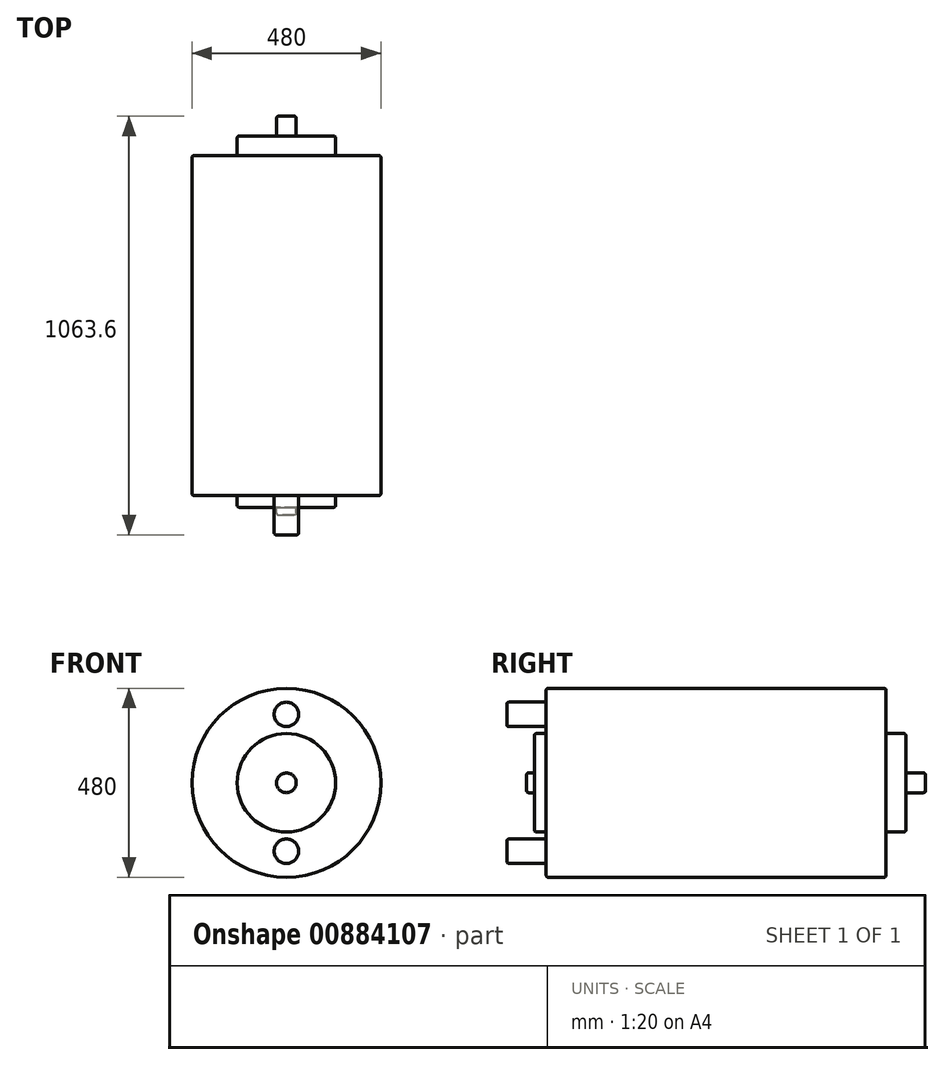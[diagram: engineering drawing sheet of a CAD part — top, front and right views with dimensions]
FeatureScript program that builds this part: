
annotation { "Feature Type Name" : "Feature", "Feature Type Description" : "" }
export const myFeature = defineFeature(function(context is Context, id is Id, definition is map)
    precondition{}
    {
        {
            var Q0;
            Q0=qCreatedBy(makeId("Right.planeOp"),FACE);
            var sketch = newSketch(context, id + "F0", { "sketchPlane" : qUnion([Q0])});
            skLineSegment(sketch, "E0", {"start": v(-50, 0) * mm, "end": v(-50, 25) * mm});
            skLineSegment(sketch, "E1", {"start": v(-50, 25) * mm, "end": v(-30, 25) * mm});
            skLineSegment(sketch, "E2", {"start": v(-30, 25) * mm, "end": v(-30, 125) * mm});
            skLineSegment(sketch, "E3", {"start": v(-30, 125) * mm, "end": v(0, 125) * mm});
            skLineSegment(sketch, "E4", {"start": v(0, 125) * mm, "end": v(0, 240) * mm});
            skLineSegment(sketch, "E5", {"start": v(0, 240) * mm, "end": v(863.6, 240) * mm});
            skLineSegment(sketch, "E6", {"start": v(863.6, 240) * mm, "end": v(863.6, 125) * mm});
            skLineSegment(sketch, "E7", {"start": v(863.6, 125) * mm, "end": v(913.6, 125) * mm});
            skLineSegment(sketch, "E8", {"start": v(913.6, 125) * mm, "end": v(913.6, 25) * mm});
            skLineSegment(sketch, "E9", {"start": v(913.6, 25) * mm, "end": v(963.6, 25) * mm});
            skLineSegment(sketch, "E10", {"start": v(963.6, 25) * mm, "end": v(963.6, 0) * mm});
            skLineSegment(sketch, "E11", {"start": v(963.6, 0) * mm, "end": v(-50, 0) * mm});
            skSolve(sketch);
        }
        {
            var Q0;
            Q0 = qSketchRegion(id + "F0", true);
            var Q1;
            Q1=sQuery(id+"F0.wireOp",EDGE,"E11");
            revolve(context, id + "F1", {"surfaceOperationType" : NewSurfaceOperationType.NEW, "entities" : qUnion([Q0]), "axis" : qUnion([Q1]), "revolveType" : RevolveType.FULL});
        }
        {
            var Q0;
            Q0=makeQuery(id+"F1.opRevolve","SWEPT_EDGE",EDGE,{"disambiguationData":[OSD([sQuery(id+"F0.wireOp",EDGE,"E5"),sQuery(id+"F0.wireOp",EDGE,"E6")])]});
            var Q1;
            Q1=makeQuery(id+"F1.opRevolve","SWEPT_EDGE",EDGE,{"disambiguationData":[OSD([sQuery(id+"F0.wireOp",EDGE,"E7"),sQuery(id+"F0.wireOp",EDGE,"E8")])]});
            var Q2;
            Q2=makeQuery(id+"F1.opRevolve","SWEPT_EDGE",EDGE,{"disambiguationData":[OSD([sQuery(id+"F0.wireOp",EDGE,"E9"),sQuery(id+"F0.wireOp",EDGE,"E10")])]});
            var Q3;
            Q3=makeQuery(id+"F1.opRevolve","SWEPT_EDGE",EDGE,{"disambiguationData":[OSD([sQuery(id+"F0.wireOp",EDGE,"E4"),sQuery(id+"F0.wireOp",EDGE,"E5")])]});
            var Q4;
            Q4=makeQuery(id+"F1.opRevolve","SWEPT_EDGE",EDGE,{"disambiguationData":[OSD([sQuery(id+"F0.wireOp",EDGE,"E2"),sQuery(id+"F0.wireOp",EDGE,"E3")])]});
            var Q5;
            Q5=makeQuery(id+"F1.opRevolve","SWEPT_EDGE",EDGE,{"disambiguationData":[OSD([sQuery(id+"F0.wireOp",EDGE,"E0"),sQuery(id+"F0.wireOp",EDGE,"E1")])]});
            fillet(context, id + "F2", {"entities" : qUnion([Q0, Q1, Q2, Q3, Q4, Q5]), "radius" : 5.08 * mm, "tangentPropagation" : true, "allowEdgeOverflow" : false});
        }
        {
            var Q0;
            Q0=makeQuery(id+"F1.opRevolve","SWEPT_FACE",FACE,{"disambiguationData":[OSD([sQuery(id+"F0.wireOp",EDGE,"E4")])]});
            var sketch = newSketch(context, id + "F3", { "sketchPlane" : qUnion([Q0])});
            skCircle(sketch, "E12", {"center": v(0, -173.89) * mm, "radius": 31 * mm});
            skLineSegment(sketch, "E13", {"start": v(0, 0) * mm, "end": v(0, 173.89) * mm});
            skCircle(sketch, "E14", {"center": v(0, 173.89) * mm, "radius": 31 * mm});
            skSolve(sketch);
        }
        {
            var Q0;
            Q0=makeQuery(id+"F3.imprint","IMPRINT",FACE,{"disambiguationData":[TD([[makeQuery(id+"F3.imprint","IMPRINT",EDGE,{"derivedFrom":sQuery(id+"F3.wireOp",EDGE,"E14")}),1.0]])]});
            var Q1;
            Q1=makeQuery(id+"F3.imprint","IMPRINT",FACE,{"disambiguationData":[TD([[makeQuery(id+"F3.imprint","IMPRINT",EDGE,{"derivedFrom":sQuery(id+"F3.wireOp",EDGE,"E12")}),1.0]])]});
            extrude(context, id + "F4", {"entities" : qUnion([Q0, Q1]), "operationType" : NewBodyOperationType.ADD, "depth" : 100 * mm, "offsetDistance" : 25.4 * mm});
        }
        {
            var Q0;
            Q0=makeQuery(id+"F4.opExtrude","CAP_EDGE",EDGE,{"disambiguationData":[OSD([sQuery(id+"F3.wireOp",EDGE,"E12")])],"isStart":false});
            var Q1;
            Q1=makeQuery(id+"F4.opExtrude","CAP_EDGE",EDGE,{"disambiguationData":[OSD([sQuery(id+"F3.wireOp",EDGE,"E14")])],"isStart":false});
            fillet(context, id + "F5", {"entities" : qUnion([Q0, Q1]), "radius" : 5.08 * mm, "tangentPropagation" : true, "allowEdgeOverflow" : false});
        }
    });
